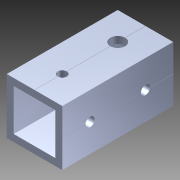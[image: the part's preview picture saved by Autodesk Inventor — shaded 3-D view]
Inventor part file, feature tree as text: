
AUTODESK INVENTOR PART (.ipt)
format: ipt  version: 2014 (Build 180170000, 170)  size: 1,173,504 bytes
history: native  units: in
note: dims shown in document units (in); Inventor stores cm internally (conversion verified against a paired STEP export)
features: extrude x2, sketch x2, pattern_circular x1, other x1, plane x1, imported_body x1
ambient origin geometry x8: Origin, YZ Plane, XZ Plane, XY Plane, X Axis, Y Axis, Z Axis, Center Point
bodies: Body1 (feature_tree)
feature tree (8):
  pattern_circular  "CirPattern2"
  other  "217-3426-STEP1"
  plane  "Work Plane1"
  extrude  "Extrusion1"  Depth=3937.0079in TaperAngle=0.0deg
  extrude  "Extrusion3"  Depth=1.0in TaperAngle=0.0deg
  imported_body  "Base1"
  sketch  "Sketch1"  dims[d0=-2.0in d1=3937.0079in d2=0.0in]
  sketch  "Sketch4"  dims[d6=0.266in d7=1.0in d8=0.0in]
